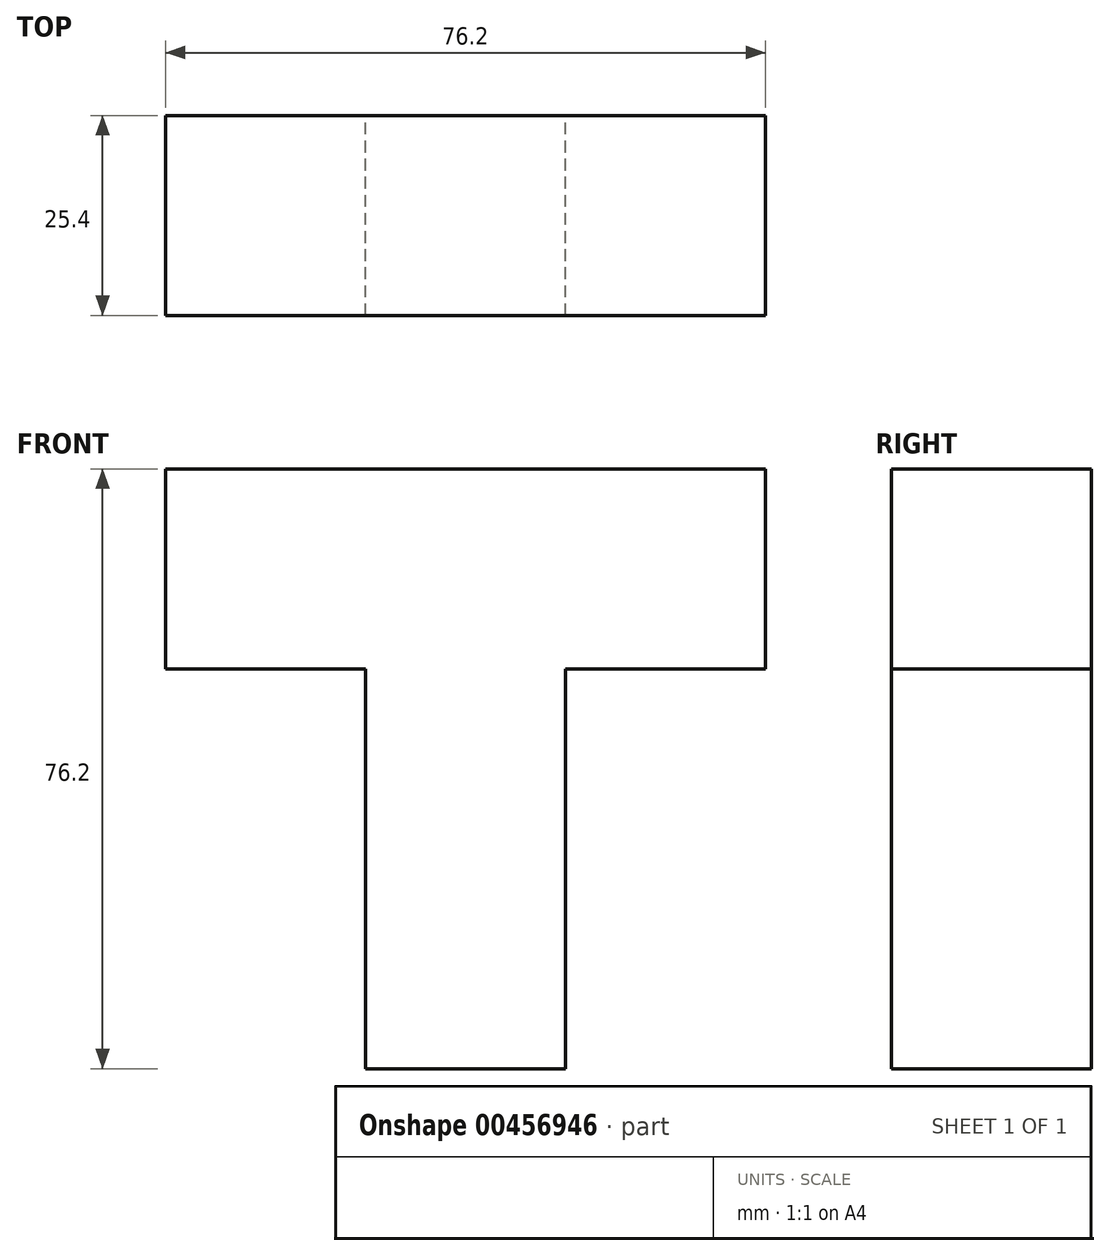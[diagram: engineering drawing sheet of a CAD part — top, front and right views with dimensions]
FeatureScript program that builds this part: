
annotation { "Feature Type Name" : "Feature", "Feature Type Description" : "" }
export const myFeature = defineFeature(function(context is Context, id is Id, definition is map)
    precondition{}
    {
        {
            var Q0;
            Q0=qCreatedBy(makeId("Front.planeOp"),FACE);
            var sketch = newSketch(context, id + "F0", { "sketchPlane" : qUnion([Q0])});
            skLineSegment(sketch, "E0", {"start": v(0, 0) * mm, "end": v(0, 50.8) * mm});
            skLineSegment(sketch, "E1", {"start": v(0, 50.8) * mm, "end": v(-25.4, 50.8) * mm});
            skLineSegment(sketch, "E2", {"start": v(-25.4, 50.8) * mm, "end": v(-25.4, 76.2) * mm});
            skLineSegment(sketch, "E3", {"start": v(-25.4, 76.2) * mm, "end": v(50.8, 76.2) * mm});
            skLineSegment(sketch, "E4", {"start": v(50.8, 76.2) * mm, "end": v(50.8, 50.8) * mm});
            skLineSegment(sketch, "E5", {"start": v(50.8, 50.8) * mm, "end": v(25.4, 50.8) * mm});
            skLineSegment(sketch, "E6", {"start": v(25.4, 50.8) * mm, "end": v(25.4, 0) * mm});
            skLineSegment(sketch, "E7", {"start": v(25.4, 0) * mm, "end": v(0, 0) * mm});
            skSolve(sketch);
        }
        {
            var Q0;
            Q0=makeQuery(id+"F0.imprint","IMPRINT",FACE,{"disambiguationData":[TD([[makeQuery(id+"F0.imprint","IMPRINT",EDGE,{"derivedFrom":sQuery(id+"F0.wireOp",EDGE,"E0")}),-1.0]])]});
            extrude(context, id + "F1", {"entities" : qUnion([Q0]), "endBound" : BoundingType.SYMMETRIC, "depth" : 25.4 * mm});
        }
    });
